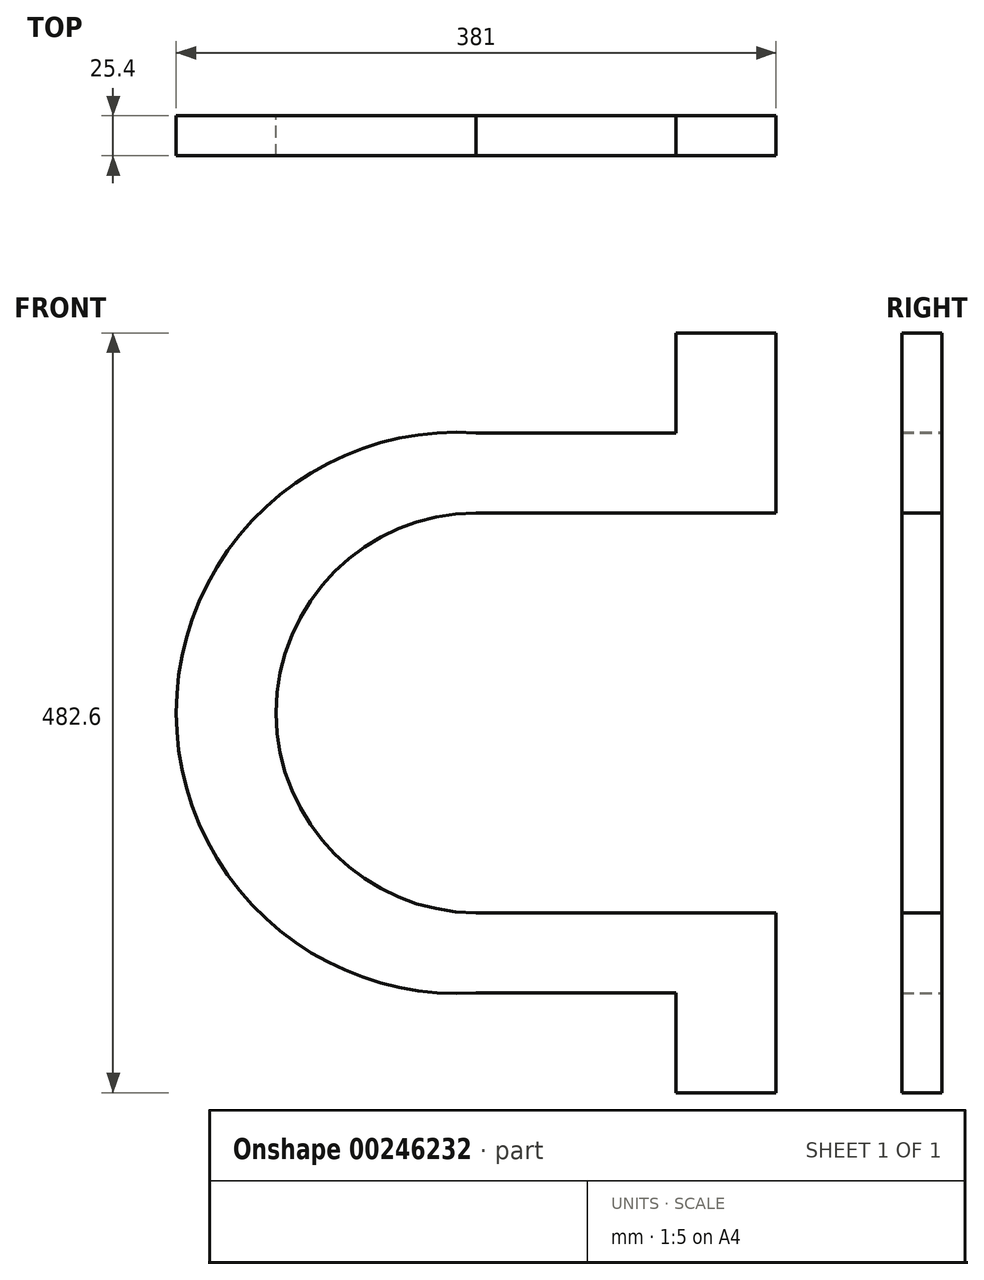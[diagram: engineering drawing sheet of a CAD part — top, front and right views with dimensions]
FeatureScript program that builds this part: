
annotation { "Feature Type Name" : "Feature", "Feature Type Description" : "" }
export const myFeature = defineFeature(function(context is Context, id is Id, definition is map)
    precondition{}
    {
        {
            var Q0;
            Q0=qCreatedBy(makeId("Front.planeOp"),FACE);
            var sketch = newSketch(context, id + "F0", { "sketchPlane" : qUnion([Q0])});
            skLineSegment(sketch, "E0.bottom", {"start": v(127, -177.8) * mm, "end": v(-24.55, -177.8) * mm});
            skLineSegment(sketch, "E0.top", {"start": v(127, 177.8) * mm, "end": v(-24.55, 177.8) * mm});
            skLineSegment(sketch, "E0.left", {"start": v(190.5, -177.8) * mm, "end": v(190.5, -127) * mm});
            skPoint(sketch, "E0.middle", {"position": v(0, 0) * mm});
            skArc(sketch, "E1", {"start": v(0, 127) * mm, "mid": v(-127, 0) * mm, "end": v(0, -127) * mm});
            skLineSegment(sketch, "E2", {"start": v(0, 127) * mm, "end": v(190.5, 127) * mm});
            skLineSegment(sketch, "E3", {"start": v(0, -127) * mm, "end": v(190.5, -127) * mm});
            skLineSegment(sketch, "E4.top", {"start": v(190.5, -241.3) * mm, "end": v(127, -241.3) * mm});
            skLineSegment(sketch, "E4.left", {"start": v(190.5, -177.8) * mm, "end": v(190.5, -241.3) * mm});
            skLineSegment(sketch, "E4.right", {"start": v(127, -177.8) * mm, "end": v(127, -241.3) * mm});
            skPoint(sketch, "E4.middle", {"position": v(158.75, -209.55) * mm});
            skLineSegment(sketch, "E5.top", {"start": v(190.5, 241.3) * mm, "end": v(127, 241.3) * mm});
            skLineSegment(sketch, "E5.left", {"start": v(190.5, 177.8) * mm, "end": v(190.5, 241.3) * mm});
            skLineSegment(sketch, "E5.right", {"start": v(127, 177.8) * mm, "end": v(127, 241.3) * mm});
            skPoint(sketch, "E5.middle", {"position": v(158.75, 209.55) * mm});
            skLineSegment(sketch, "E6.trimOffspring", {"start": v(190.5, 127) * mm, "end": v(190.5, 177.8) * mm});
            skArc(sketch, "E7", {"start": v(0, 177.8) * mm, "mid": v(-190.5, 0) * mm, "end": v(0, -177.8) * mm});
            skPoint(sketch, "E7.first.point", {"position": v(0, -177.8) * mm});
            skPoint(sketch, "E7.second.point", {"position": v(-190.5, 0) * mm});
            skPoint(sketch, "E7.third.point", {"position": v(0, 177.8) * mm});
            skPoint(sketch, "E8.orphan", {"position": v(-190.5, -177.8) * mm});
            skPoint(sketch, "E9.orphan", {"position": v(-190.5, 177.8) * mm});
            skSolve(sketch);
        }
        {
            var Q0;
            Q0 = qSketchRegion(id + "F0", true);
            extrude(context, id + "F1", {"entities" : qUnion([Q0]), "depth" : 25.4 * mm});
        }
    });
